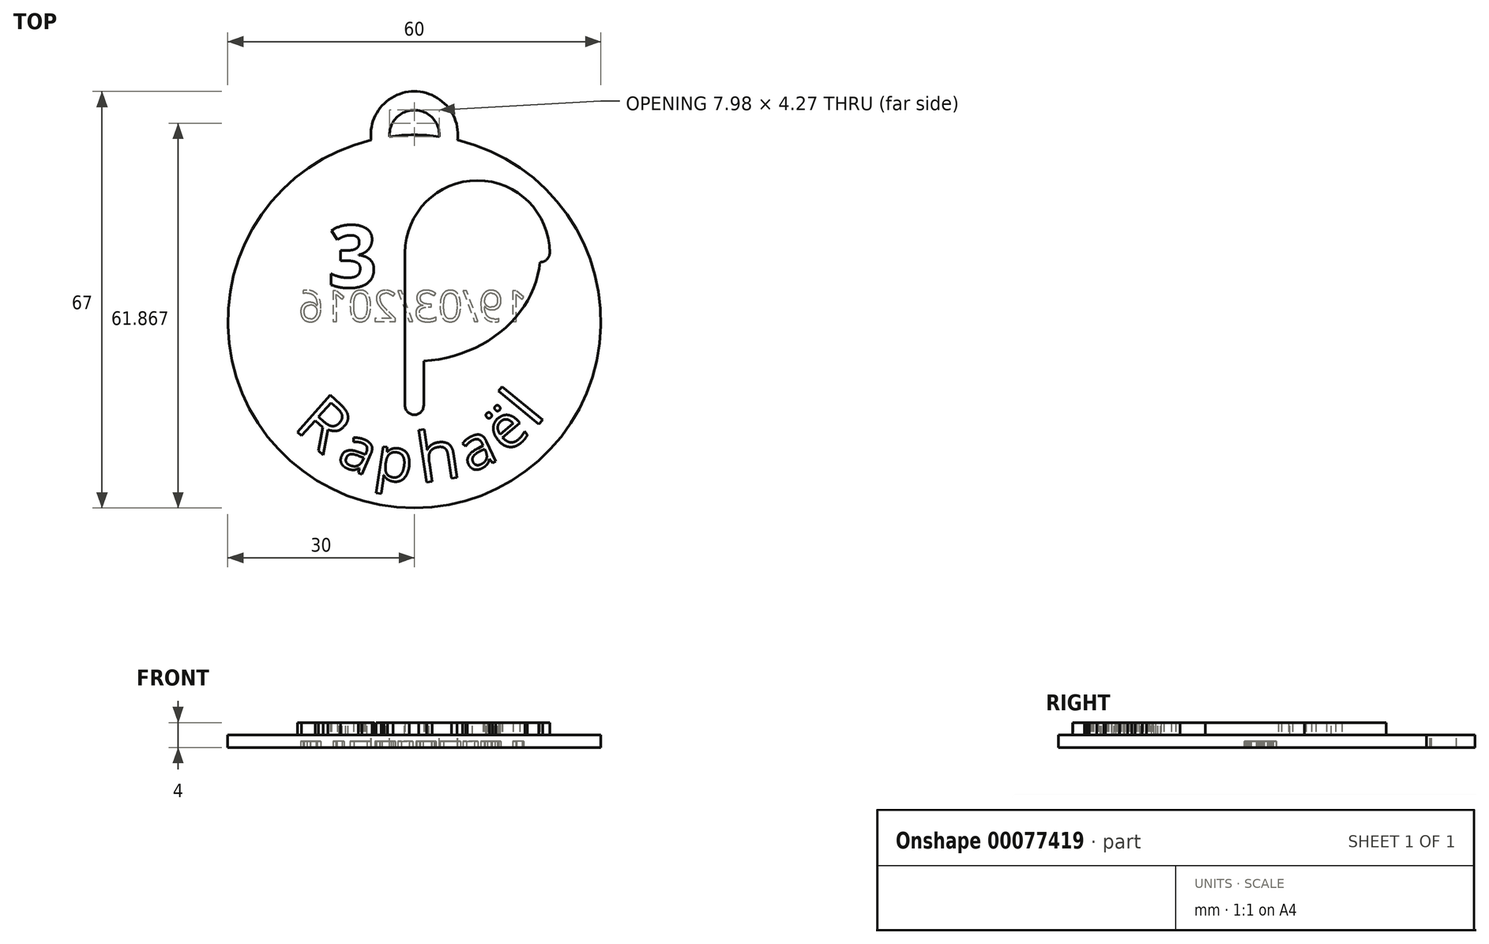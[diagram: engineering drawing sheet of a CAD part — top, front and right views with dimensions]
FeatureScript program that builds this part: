
annotation { "Feature Type Name" : "Feature", "Feature Type Description" : "" }
export const myFeature = defineFeature(function(context is Context, id is Id, definition is map)
    precondition{}
    {
        {
            var Q0;
            Q0=qCreatedBy(makeId("Top.planeOp"),FACE);
            var sketch = newSketch(context, id + "F0", { "sketchPlane" : qUnion([Q0])});
            skCircle(sketch, "E0", {"center": v(0, 0) * mm, "radius": 30 * mm});
            skSolve(sketch);
        }
        {
            var Q0;
            Q0=qSketchRegion(id+"F0",true);
            extrude(context, id + "F1", {"entities" : qUnion([Q0]), "oppositeDirection" : true, "depth" : 2 * mm});
        }
        {
            var Q0;
            Q0=qCreatedBy(makeId("Top.planeOp"),FACE);
            var sketch = newSketch(context, id + "F2", { "sketchPlane" : qUnion([Q0])});
            skEllipticalArc(sketch, "E1", {});
            skLineSegment(sketch, "E2", {"start": v(0, 0) * mm, "end": v(0, 30) * mm, "construction": true});
            skLineSegment(sketch, "E3", {"start": v(0, 11.04) * mm, "end": v(0, -13.5) * mm});
            skArc(sketch, "E4", {"start": v(20.27, 11.04) * mm, "mid": v(10.13, 21.17) * mm, "end": v(0, 11.04) * mm});
            skLineSegment(sketch, "E5", {"start": v(0, 11.04) * mm, "end": v(-16.84, 20.76) * mm, "construction": true});
            skLineSegment(sketch, "E6", {"start": v(0, 11.04) * mm, "end": v(-20.27, 11.04) * mm, "construction": true});
            skArc(sketch, "E7.0.startCap", {"start": v(-1.5, 11.04) * mm, "mid": v(0, 12.54) * mm, "end": v(1.5, 11.04) * mm});
            skArc(sketch, "E7.0.endCap", {"start": v(1.5, -13.5) * mm, "mid": v(0, -15) * mm, "end": v(-1.5, -13.5) * mm});
            skLineSegment(sketch, "E7.0.left", {"start": v(1.5, 11.04) * mm, "end": v(1.5, -13.5) * mm});
            skLineSegment(sketch, "E7.0.right", {"start": v(-1.5, 11.04) * mm, "end": v(-1.5, -13.5) * mm});
            skArc(sketch, "E8.0.startCap", {"start": v(21.77, 11.04) * mm, "mid": v(20.27, 9.54) * mm, "end": v(18.77, 11.04) * mm});
            skArc(sketch, "E8.0.endCap", {"start": v(1.5, 11.04) * mm, "mid": v(0, 9.54) * mm, "end": v(-1.5, 11.04) * mm});
            skArc(sketch, "E8.0.left", {"start": v(18.77, 11.04) * mm, "mid": v(10.13, 19.67) * mm, "end": v(1.5, 11.04) * mm});
            skArc(sketch, "E8.0.right", {"start": v(21.77, 11.04) * mm, "mid": v(10.13, 22.67) * mm, "end": v(-1.5, 11.04) * mm});
            skArc(sketch, "E8.1.startCap", {"start": v(-18.02, 21.68) * mm, "mid": v(-15.91, 21.95) * mm, "end": v(-15.65, 19.84) * mm});
            skArc(sketch, "E8.1.endCap", {"start": v(18.77, 11.04) * mm, "mid": v(20.27, 12.54) * mm, "end": v(21.77, 11.04) * mm});
            skFitSpline(sketch, "E8.1.left", {"points": [v(18.7, 9.5) * mm, v(18.8, 11.04) * mm, v(18.7, 12.6) * mm, v(18.36, 14.63) * mm, v(17.66, 16.6) * mm, v(16.63, 18.49) * mm, v(15.37, 20.3) * mm, v(13.44, 22.32) * mm, v(11.07, 24) * mm, v(8.94, 25.1) * mm, v(6.7, 26.01) * mm, v(4.32, 26.63) * mm, v(1.87, 26.95) * mm, v(0, 27.03) * mm, v(-1.87, 26.95) * mm, v(-4.32, 26.63) * mm, v(-6.7, 26.01) * mm, v(-8.94, 25.1) * mm, v(-11.07, 24) * mm, v(-13.44, 22.32) * mm, v(-15.37, 20.3) * mm, v(-16.63, 18.49) * mm, v(-17.66, 16.6) * mm, v(-18.36, 14.63) * mm, v(-18.7, 12.6) * mm, v(-18.8, 11.04) * mm, v(-18.7, 9.5) * mm, v(-18.36, 7.46) * mm, v(-17.66, 5.48) * mm, v(-16.63, 3.6) * mm, v(-15.37, 1.8) * mm, v(-13.44, -0.24) * mm, v(-11.07, -1.92) * mm, v(-8.94, -3.02) * mm, v(-6.7, -3.93) * mm, v(-4.32, -4.55) * mm, v(-1.87, -4.86) * mm, v(0, -4.94) * mm, v(1.87, -4.86) * mm, v(4.32, -4.55) * mm, v(6.7, -3.93) * mm, v(8.94, -3.02) * mm, v(11.07, -1.92) * mm, v(13.44, -0.24) * mm, v(15.37, 1.8) * mm, v(16.63, 3.6) * mm, v(17.66, 5.48) * mm, v(18.36, 7.46) * mm, v(18.7, 9.5) * mm, v(18.8, 11.04) * mm, v(18.7, 12.6) * mm]});
            skFitSpline(sketch, "E8.1.right", {"points": [v(21.7, 9.15) * mm, v(21.8, 11.04) * mm, v(21.7, 12.93) * mm, v(21.27, 15.42) * mm, v(20.42, 17.81) * mm, v(19.18, 20.07) * mm, v(17.69, 22.22) * mm, v(15.4, 24.61) * mm, v(12.65, 26.56) * mm, v(10.2, 27.83) * mm, v(7.62, 28.88) * mm, v(4.92, 29.58) * mm, v(2.12, 29.94) * mm, v(0, 30.03) * mm, v(-2.12, 29.94) * mm, v(-4.92, 29.58) * mm, v(-7.62, 28.88) * mm, v(-10.2, 27.83) * mm, v(-12.65, 26.56) * mm, v(-15.4, 24.61) * mm, v(-17.69, 22.22) * mm, v(-19.18, 20.07) * mm, v(-20.42, 17.81) * mm, v(-21.27, 15.42) * mm, v(-21.7, 12.93) * mm, v(-21.8, 11.04) * mm, v(-21.7, 9.15) * mm, v(-21.27, 6.67) * mm, v(-20.42, 4.27) * mm, v(-19.18, 2) * mm, v(-17.69, -0.14) * mm, v(-15.4, -2.53) * mm, v(-12.65, -4.48) * mm, v(-10.2, -5.75) * mm, v(-7.62, -6.8) * mm, v(-4.92, -7.5) * mm, v(-2.12, -7.86) * mm, v(0, -7.95) * mm, v(2.12, -7.86) * mm, v(4.92, -7.5) * mm, v(7.62, -6.8) * mm, v(10.2, -5.75) * mm, v(12.65, -4.48) * mm, v(15.4, -2.53) * mm, v(17.69, -0.14) * mm, v(19.18, 2) * mm, v(20.42, 4.27) * mm, v(21.27, 6.67) * mm, v(21.7, 9.15) * mm, v(21.8, 11.04) * mm, v(21.7, 12.93) * mm]});
            const initialGuessF2  = {"E1": [0, 0.011041626236194823, 1, 0, 0.020266667008310185, 0.017458373763805178, 2.5511335140588507, 0]};
            skSetInitialGuess(sketch, initialGuessF2);
            skSolve(sketch);
        }
        {
            var Q0;
            {var subQ0=sQuery(id+"F2.wireOp",EDGE,"E8.1.startCap");Q0=makeQuery(id+"F2.imprint","IMPRINT",FACE,{"disambiguationData":[TD([[makeQuery(id+"F2.imprint","IMPRINT",EDGE,{"derivedFrom":subQ0}),-1.0]])]});}
            var Q1;
            {var subQ0=sQuery(id+"F2.wireOp",EDGE,"E7.0.right");var subQ1=sQuery(id+"F2.wireOp",EDGE,"E1");var subQ2=makeQuery(id+"F2.imprint","INTERSECT",VERTEX,{"derivedFrom":[subQ1,subQ0]});Q1=makeQuery(id+"F2.imprint","IMPRINT",FACE,{"disambiguationData":[TD([[makeQuery(id+"F2.imprint","IMPRINT",EDGE,{"disambiguationData":[TD([[subQ2,-1.0]])],"derivedFrom":subQ1}),1.0]])]});}
            var Q2;
            {var subQ0=sQuery(id+"F2.wireOp",EDGE,"E3");var subQ1=sQuery(id+"F2.wireOp",EDGE,"E1");var subQ2=makeQuery(id+"F2.imprint","INTERSECT",VERTEX,{"derivedFrom":[subQ1,subQ0]});Q2=makeQuery(id+"F2.imprint","IMPRINT",FACE,{"disambiguationData":[TD([[makeQuery(id+"F2.imprint","IMPRINT",EDGE,{"disambiguationData":[TD([[subQ2,-1.0]])],"derivedFrom":subQ1}),1.0]])]});}
            var Q3;
            {var subQ0=sQuery(id+"F2.wireOp",EDGE,"E7.0.right");var subQ1=sQuery(id+"F2.wireOp",EDGE,"E1");var subQ2=makeQuery(id+"F2.imprint","INTERSECT",VERTEX,{"derivedFrom":[subQ1,subQ0]});Q3=makeQuery(id+"F2.imprint","IMPRINT",FACE,{"disambiguationData":[TD([[makeQuery(id+"F2.imprint","IMPRINT",EDGE,{"disambiguationData":[TD([[subQ2,-1.0]])],"derivedFrom":subQ1}),-1.0]])]});}
            var Q4;
            {var subQ0=sQuery(id+"F2.wireOp",EDGE,"E3");var subQ1=sQuery(id+"F2.wireOp",EDGE,"E1");var subQ2=makeQuery(id+"F2.imprint","INTERSECT",VERTEX,{"derivedFrom":[subQ1,subQ0]});Q4=makeQuery(id+"F2.imprint","IMPRINT",FACE,{"disambiguationData":[TD([[makeQuery(id+"F2.imprint","IMPRINT",EDGE,{"disambiguationData":[TD([[subQ2,-1.0]])],"derivedFrom":subQ1}),-1.0]])]});}
            var Q5;
            {var subQ0=sQuery(id+"F2.wireOp",EDGE,"E7.0.left");var subQ1=sQuery(id+"F2.wireOp",EDGE,"E1");var subQ2=makeQuery(id+"F2.imprint","INTERSECT",VERTEX,{"derivedFrom":[subQ1,subQ0]});Q5=makeQuery(id+"F2.imprint","IMPRINT",FACE,{"disambiguationData":[TD([[makeQuery(id+"F2.imprint","IMPRINT",EDGE,{"disambiguationData":[TD([[subQ2,-1.0]])],"derivedFrom":subQ1}),-1.0]])]});}
            var Q6;
            {var subQ0=sQuery(id+"F2.wireOp",EDGE,"E7.0.left");var subQ1=sQuery(id+"F2.wireOp",EDGE,"E1");var subQ2=makeQuery(id+"F2.imprint","INTERSECT",VERTEX,{"derivedFrom":[subQ1,subQ0]});Q6=makeQuery(id+"F2.imprint","IMPRINT",FACE,{"disambiguationData":[TD([[makeQuery(id+"F2.imprint","IMPRINT",EDGE,{"disambiguationData":[TD([[subQ2,-1.0]])],"derivedFrom":subQ1}),1.0]])]});}
            var Q7;
            {var subQ0=sQuery(id+"F2.wireOp",EDGE,"E4");var subQ1=sQuery(id+"F2.wireOp",EDGE,"E1");var subQ2=makeQuery(id+"F2.imprint","INTERSECT",VERTEX,{"derivedFrom":[subQ1,subQ0]});Q7=makeQuery(id+"F2.imprint","IMPRINT",FACE,{"disambiguationData":[TD([[makeQuery(id+"F2.imprint","IMPRINT",EDGE,{"disambiguationData":[TD([[subQ2,1.0]])],"derivedFrom":subQ1}),-1.0]])]});}
            var Q8;
            {var subQ0=sQuery(id+"F2.wireOp",EDGE,"E4");var subQ1=sQuery(id+"F2.wireOp",EDGE,"E1");var subQ2=makeQuery(id+"F2.imprint","INTERSECT",VERTEX,{"derivedFrom":[subQ1,subQ0]});Q8=makeQuery(id+"F2.imprint","IMPRINT",FACE,{"disambiguationData":[TD([[makeQuery(id+"F2.imprint","IMPRINT",EDGE,{"disambiguationData":[TD([[subQ2,1.0]])],"derivedFrom":subQ1}),1.0]])]});}
            var Q9;
            {var subQ5=sQuery(id+"F2.wireOp",EDGE,"E8.0.left");Q9=makeQuery(id+"F2.imprint","IMPRINT",FACE,{"disambiguationData":[TD([[makeQuery(id+"F2.imprint","IMPRINT",EDGE,{"derivedFrom":subQ5}),-1.0]])]});}
            var Q10;
            {var subQ5=sQuery(id+"F2.wireOp",EDGE,"E8.0.right");Q10=makeQuery(id+"F2.imprint","IMPRINT",FACE,{"disambiguationData":[TD([[makeQuery(id+"F2.imprint","IMPRINT",EDGE,{"derivedFrom":subQ5}),1.0]])]});}
            var Q11;
            {var subQ0=sQuery(id+"F2.wireOp",EDGE,"E4");var subQ1=sQuery(id+"F2.wireOp",EDGE,"E3");var subQ2=makeQuery(id+"F2.imprint","INTERSECT",VERTEX,{"derivedFrom":[subQ1,subQ0]});Q11=makeQuery(id+"F2.imprint","IMPRINT",FACE,{"disambiguationData":[TD([[makeQuery(id+"F2.imprint","IMPRINT",EDGE,{"disambiguationData":[TD([[subQ2,-1.0]])],"derivedFrom":subQ1}),-1.0]])]});}
            var Q12;
            {var subQ0=sQuery(id+"F2.wireOp",EDGE,"E4");var subQ1=sQuery(id+"F2.wireOp",EDGE,"E3");var subQ2=makeQuery(id+"F2.imprint","INTERSECT",VERTEX,{"derivedFrom":[subQ1,subQ0]});Q12=makeQuery(id+"F2.imprint","IMPRINT",FACE,{"disambiguationData":[TD([[makeQuery(id+"F2.imprint","IMPRINT",EDGE,{"disambiguationData":[TD([[subQ2,-1.0]])],"derivedFrom":subQ1}),1.0]])]});}
            var Q13;
            {var subQ0=sQuery(id+"F2.wireOp",EDGE,"E8.0.endCap");var subQ1=sQuery(id+"F2.wireOp",EDGE,"E3");var subQ2=makeQuery(id+"F2.imprint","INTERSECT",VERTEX,{"derivedFrom":[subQ1,subQ0]});Q13=makeQuery(id+"F2.imprint","IMPRINT",FACE,{"disambiguationData":[TD([[makeQuery(id+"F2.imprint","IMPRINT",EDGE,{"disambiguationData":[TD([[subQ2,-1.0]])],"derivedFrom":subQ1}),-1.0]])]});}
            var Q14;
            {var subQ0=sQuery(id+"F2.wireOp",EDGE,"E8.0.endCap");var subQ1=sQuery(id+"F2.wireOp",EDGE,"E3");var subQ2=makeQuery(id+"F2.imprint","INTERSECT",VERTEX,{"derivedFrom":[subQ1,subQ0]});Q14=makeQuery(id+"F2.imprint","IMPRINT",FACE,{"disambiguationData":[TD([[makeQuery(id+"F2.imprint","IMPRINT",EDGE,{"disambiguationData":[TD([[subQ2,-1.0]])],"derivedFrom":subQ1}),1.0]])]});}
            var Q15;
            {var subQ1=sQuery(id+"F2.wireOp",EDGE,"E7.0.endCap");Q15=makeQuery(id+"F2.imprint","IMPRINT",FACE,{"disambiguationData":[TD([[makeQuery(id+"F2.imprint","IMPRINT",EDGE,{"derivedFrom":subQ1}),-1.0]])]});}
            extrude(context, id + "F3", {"entities" : qUnion([Q0, Q1, Q2, Q3, Q4, Q5, Q6, Q7, Q8, Q9, Q10, Q11, Q12, Q13, Q14, Q15]), "operationType" : NewBodyOperationType.ADD, "depth" : 2 * mm});
        }
        {
            var Q0;
            Q0=qCreatedBy(makeId("Top.planeOp"),FACE);
            var sketch = newSketch(context, id + "F4", { "sketchPlane" : qUnion([Q0])});
            skText(sketch, "E9", { "text": "3", "fontName": "OpenSans-Bold.ttf"});
            skText(sketch, "E10", { "text": "D", "fontName": "OpenSans-Bold.ttf"});
            const initialGuessF4  = {"E9": [-0.0139, 0.0055, 1, 0, 0.01], "E10": [0.0055, 0.0055, 1, 0, 0.01]};
            skSetInitialGuess(sketch, initialGuessF4);
            skSolve(sketch);
        }
        {
            var Q0;
            Q0=qSketchRegion(id+"F4",true);
            extrude(context, id + "F5", {"entities" : qUnion([Q0]), "operationType" : NewBodyOperationType.ADD, "depth" : 2 * mm});
        }
        {
            var Q0;
            {var subQ8=sQuery(id+"F0.wireOp",EDGE,"E0");Q0=makeQuery(id+"F3.boolean.opBoolean","SPLIT",FACE,{"disambiguationData":[TD([makeQuery(id+"F1.opExtrude","SWEPT_FACE",FACE,{"disambiguationData":[OSD([subQ8])]})])],"derivedFrom":makeQuery(id+"F1.opExtrude","CAP_FACE",FACE,{"disambiguationData":[OSD([subQ8])],"isStart":true})});}
            var sketch = newSketch(context, id + "F6", { "sketchPlane" : qUnion([Q0])});
            skCircle(sketch, "E11.0", {"center": v(0, 0) * mm, "radius": 26 * mm, "construction": true});
            skText(sketch, "E12", { "text": "R", "fontName": "OpenSans-Regular.ttf"});
            skText(sketch, "E13", { "text": "a", "fontName": "OpenSans-Regular.ttf"});
            skText(sketch, "E14", { "text": "p", "fontName": "OpenSans-Regular.ttf"});
            skText(sketch, "E15", { "text": "h", "fontName": "OpenSans-Regular.ttf"});
            skText(sketch, "E16", { "text": "a", "fontName": "OpenSans-Regular.ttf"});
            skText(sketch, "E17", { "text": "ë", "fontName": "OpenSans-Regular.ttf"});
            skText(sketch, "E18", { "text": "l", "fontName": "OpenSans-Regular.ttf"});
            const initialGuessF6  = {"E12": [-0.01963, -0.01705, 0.7472, -0.6646, 0.008], "E13": [-0.01268, -0.0227, 0.91294, -0.40808, 0.007], "E14": [-0.0066, -0.02515, 0.98845, -0.15152, 0.007], "E15": [0.00103, -0.02598, 0.98822, 0.15305, 0.008], "E16": [0.0089, -0.02443, 0.90554, 0.42426, 0.007], "E17": [0.01473, -0.02142, 0.7664, 0.64237, 0.007], "E18": [0.01943, -0.01728, 0.63752, 0.77044, 0.008]};
            skSetInitialGuess(sketch, initialGuessF6);
            skSolve(sketch);
        }
        {
            var Q0;
            Q0=qSketchRegion(id+"F6",true);
            extrude(context, id + "F7", {"entities" : qUnion([Q0]), "operationType" : NewBodyOperationType.ADD, "depth" : 2 * mm});
        }
        {
            var Q0;
            Q0=qCreatedBy(makeId("Top.planeOp"),FACE);
            var sketch = newSketch(context, id + "F8", { "sketchPlane" : qUnion([Q0])});
            skArc(sketch, "E19", {"start": v(5.48, 29.5) * mm, "mid": v(0, 35.5) * mm, "end": v(-5.48, 29.5) * mm});
            skArc(sketch, "E20.0.startCap", {"start": v(6.97, 29.36) * mm, "mid": v(5.34, 28) * mm, "end": v(3.98, 29.63) * mm});
            skArc(sketch, "E20.0.endCap", {"start": v(-3.98, 29.63) * mm, "mid": v(-5.34, 28) * mm, "end": v(-6.97, 29.36) * mm});
            skArc(sketch, "E20.0.left", {"start": v(3.98, 29.63) * mm, "mid": v(0, 34) * mm, "end": v(-3.98, 29.63) * mm});
            skArc(sketch, "E20.0.right", {"start": v(6.97, 29.36) * mm, "mid": v(0, 37) * mm, "end": v(-6.97, 29.36) * mm});
            skSolve(sketch);
        }
        {
            var Q0;
            Q0=qSketchRegion(id+"F8",true);
            extrude(context, id + "F9", {"entities" : qUnion([Q0]), "operationType" : NewBodyOperationType.ADD, "oppositeDirection" : true, "depth" : 2 * mm});
        }
        {
            var Q0;
            Q0=makeQuery(id+"F9.boolean.opBoolean","MERGE",FACE,{"derivedFrom":[makeQuery(id+"F1.opExtrude","CAP_FACE",FACE,{"disambiguationData":[OSD([sQuery(id+"F0.wireOp",EDGE,"E0")])],"isStart":false}),makeQuery(id+"F9.opExtrude","CAP_FACE",FACE,{"disambiguationData":[OSD([sQuery(id+"F8.wireOp",EDGE,"E20.0.startCap"),sQuery(id+"F8.wireOp",EDGE,"E20.0.endCap"),sQuery(id+"F8.wireOp",EDGE,"E20.0.left"),sQuery(id+"F8.wireOp",EDGE,"E20.0.right")])],"isStart":false})]});
            var sketch = newSketch(context, id + "F10", { "sketchPlane" : qUnion([Q0])});
            skText(sketch, "E21", { "text": "19/03/2016", "fontName": "OpenSans-Regular.ttf"});
            const initialGuessF10  = {"E21": [0.01826, 0, -1, 0, 0.005]};
            skSetInitialGuess(sketch, initialGuessF10);
            skSolve(sketch);
        }
        {
            var Q0;
            Q0=qSketchRegion(id+"F10",true);
            extrude(context, id + "F11", {"entities" : qUnion([Q0]), "operationType" : NewBodyOperationType.REMOVE, "oppositeDirection" : true, "depth" : 1 * mm});
        }
    });
